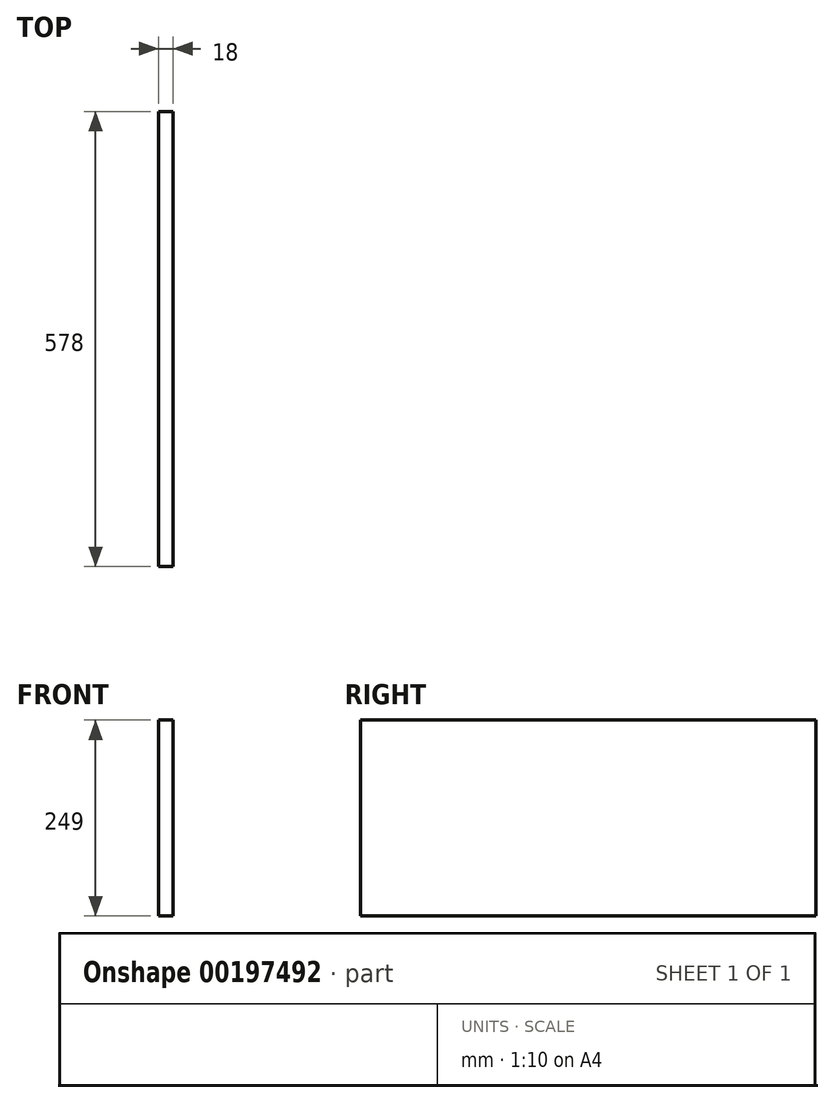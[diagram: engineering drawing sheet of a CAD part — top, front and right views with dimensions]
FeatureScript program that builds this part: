
annotation { "Feature Type Name" : "Feature", "Feature Type Description" : "" }
export const myFeature = defineFeature(function(context is Context, id is Id, definition is map)
    precondition{}
    {
        {
            var Q0;
            Q0=qCreatedBy(makeId("Right.planeOp"),FACE);
            var sketch = newSketch(context, id + "F0", { "sketchPlane" : qUnion([Q0])});
            skLineSegment(sketch, "E0.bottom", {"start": v(289, 124.5) * mm, "end": v(-289, 124.5) * mm});
            skLineSegment(sketch, "E0.top", {"start": v(289, -124.5) * mm, "end": v(-289, -124.5) * mm});
            skLineSegment(sketch, "E0.left", {"start": v(289, 124.5) * mm, "end": v(289, -124.5) * mm});
            skLineSegment(sketch, "E0.right", {"start": v(-289, 124.5) * mm, "end": v(-289, -124.5) * mm});
            skPoint(sketch, "E0.middle", {"position": v(0, 0) * mm});
            skSolve(sketch);
        }
        {
            var Q0;
            Q0 = qSketchRegion(id + "F0", true);
            extrude(context, id + "F1", {"entities" : qUnion([Q0]), "depth" : 18 * mm});
        }
    });
